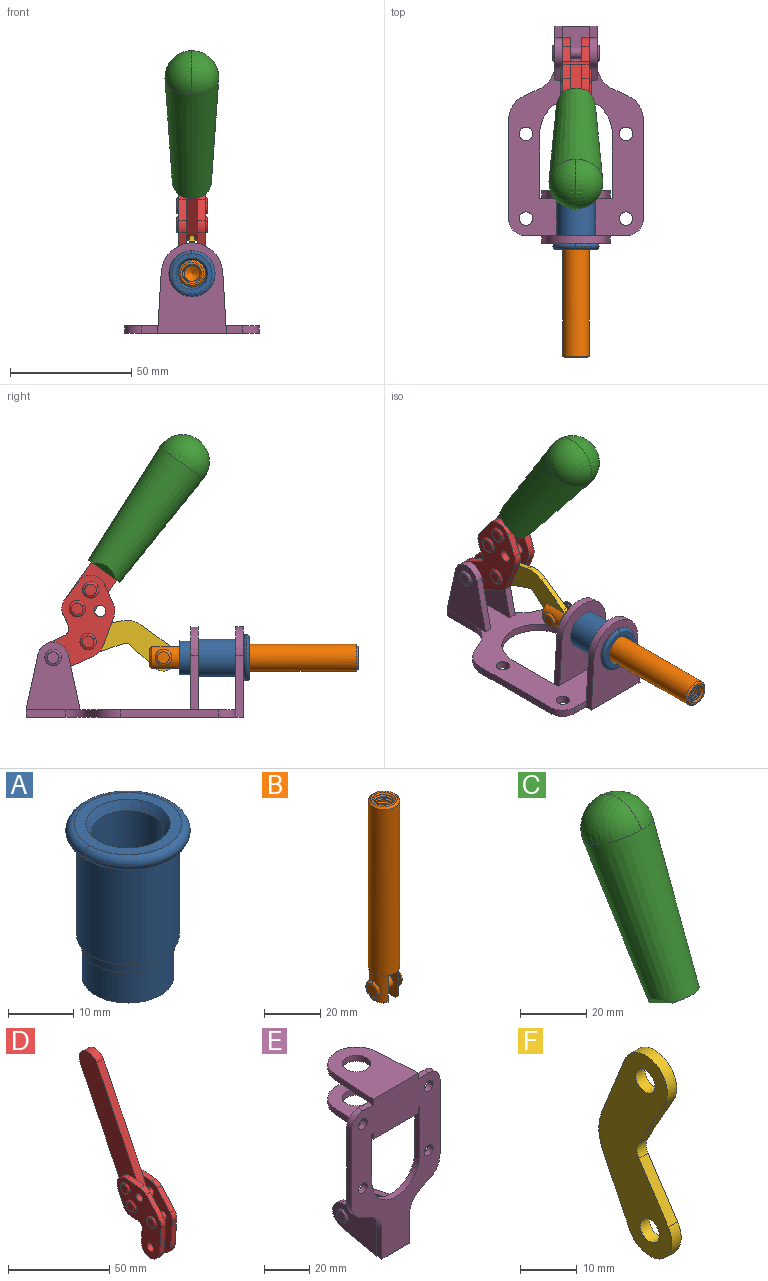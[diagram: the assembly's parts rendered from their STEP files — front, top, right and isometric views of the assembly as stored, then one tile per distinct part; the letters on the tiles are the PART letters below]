
ASSEMBLY  parts=6 mates=6
PART A: 15 faces, bbox 20.6x20.6x28.7 mm
  f0: torus R=8.26mm, axis (0,0,1), area 56.8mm2, adj f1,f10,f12
  f1: torus R=8.26mm, axis (0,0,1), area 56.8mm2, adj f0,f6,f13
  f2: cylinder r=5.59mm len=25.91mm, axis (0,0,1), area 909.6mm2, adj f3,f4
  f3: cone r=6.86mm half-angle=45deg, axis (0,0,-1), area 70.2mm2, adj f2,f14
  f4: cone r=6.47mm half-angle=30deg, axis (0,0,1), area 66.7mm2, adj f2,f13
  f5: cylinder r=7.04mm len=14.07mm, axis (0,0,1), area 252.6mm2, adj f11,f14
  f6: torus R=8.26mm, axis (0,0,1), area 56.8mm2, adj f1,f12,f13
  f7: cylinder r=7.16mm len=14.33mm, axis (0,0,1), area 91.5mm2, adj f9,f11
  f8: cylinder r=7.86mm len=18.42mm, axis (0,0,1), area 909.6mm2, adj f9,f10
  f9: plane 15.72x15.72mm, normal (0,0,-1), area 33mm2, adj f7,f8
  f10: plane 16.51x16.51mm, normal (0,0,-1), area 19.9mm2, adj f0,f8,f12
  f11: plane 14.33x14.33mm, normal (0,0,-1), area 5.7mm2, adj f5,f7
  f12: torus R=8.26mm, axis (0,0,1), area 56.8mm2, adj f0,f6,f10
  f13: plane 16.51x16.51mm, normal (0,0,1), area 82.7mm2, adj f1,f4,f6
  f14: plane 14.07x14.07mm, normal (0,0,-1), area 7.8mm2, adj f3,f5
PART B: 48 faces, bbox 12.6x11.1x86.1 mm
  f0: torus R=2.41mm, axis (-1,0,0), area 15mm2, adj f30,f32,f34
  f1: torus R=2.41mm, axis (-1,0,0), area 15mm2, adj f29,f31,f33
  f2: cylinder r=5.54mm len=72.39mm, axis (0,0,1), area 2518.5mm2, adj f3,f4,f42,f43
  f3: cone r=5.54mm half-angle=45deg, axis (0,0,1), area 7.6mm2, adj f2,f5,f41
  f4: cone r=5.54mm half-angle=45deg, axis (0,0,-1), area 34.9mm2, adj f2,f39
  f5: cylinder r=5.08mm len=11.48mm, axis (0,0,1), area 108.3mm2, adj f3,f7,f8,f41
  f6: cylinder r=2.41mm len=4.83mm, axis (-1,0,0), area 71.2mm2, adj f40,f41
  f7: cylinder r=2.41mm len=4.83mm, axis (-1,0,0), area 7.6mm2, adj f5,f34
  f8: cone r=5.08mm half-angle=45deg, axis (0,0,1), area 10.6mm2, adj f5,f37,f41
  f9: cone r=3.98mm half-angle=45deg, axis (0,0,1), area 17.6mm2, adj f27,f39,f45,f46,f47
  f10: cylinder r=2.41mm len=4.83mm, axis (-1,0,0), area 7.6mm2, adj f33,f38
  f11: cylinder r=3.2mm len=6.4mm, axis (0,0,1), area 78.4mm2, adj f12,f28,f44,f45,f47
  f12: cylinder r=3.2mm len=6.4mm, axis (0,0,1), area 10.5mm2, adj f11,f13,f45,f47
  f13: cylinder r=3.2mm len=6.4mm, axis (0,0,1), area 10.5mm2, adj f12,f14,f45,f47
  f14: cylinder r=3.2mm len=6.4mm, axis (0,0,1), area 10.5mm2, adj f13,f15,f45,f47
  f15: cylinder r=3.2mm len=6.4mm, axis (0,0,1), area 10.5mm2, adj f14,f16,f45,f47
  f16: cylinder r=3.2mm len=6.4mm, axis (0,0,1), area 10.5mm2, adj f15,f17,f45,f47
  f17: cylinder r=3.2mm len=6.4mm, axis (0,0,1), area 10.5mm2, adj f16,f18,f45,f47
  f18: cylinder r=3.2mm len=6.4mm, axis (0,0,1), area 10.5mm2, adj f17,f19,f45,f47
  f19: cylinder r=3.2mm len=6.4mm, axis (0,0,1), area 10.5mm2, adj f18,f20,f45,f47
  f20: cylinder r=3.2mm len=6.4mm, axis (0,0,1), area 10.5mm2, adj f19,f21,f45,f47
  f21: cylinder r=3.2mm len=6.4mm, axis (0,0,1), area 10.5mm2, adj f20,f22,f45,f47
  f22: cylinder r=3.2mm len=6.4mm, axis (0,0,1), area 10.5mm2, adj f21,f23,f45,f47
  f23: cylinder r=3.2mm len=6.4mm, axis (0,0,1), area 10.5mm2, adj f22,f24,f45,f47
  f24: cylinder r=3.2mm len=6.4mm, axis (0,0,1), area 10.5mm2, adj f23,f25,f45,f47
  f25: cylinder r=3.2mm len=6.4mm, axis (0,0,1), area 10.5mm2, adj f24,f26,f45,f47
  f26: cylinder r=3.2mm len=6.4mm, axis (0,0,1), area 10.5mm2, adj f25,f27,f45,f47
  f27: cylinder r=3.2mm len=6.4mm, axis (0,0,1), area 7.4mm2, adj f9,f26,f45,f47
  f28: cone r=3.2mm half-angle=60deg, axis (0,0,1), area 37.2mm2, adj f11
  f29: plane 4.83x4.83mm, normal (-1,0,0), area 18.3mm2, adj f1,f31
  f30: plane 4.83x4.83mm, normal (1,0,0), area 18.3mm2, adj f0,f32
  f31: torus R=2.41mm, axis (-1,0,0), area 15mm2, adj f1,f29,f33
  f32: torus R=2.41mm, axis (-1,0,0), area 15mm2, adj f0,f30,f34
  f33: plane 6.83x6.83mm, normal (1,0,0), area 18.3mm2, adj f1,f10,f31
  f34: plane 6.83x6.83mm, normal (-1,0,0), area 18.3mm2, adj f0,f7,f32
  f35: cone r=5.08mm half-angle=45deg, axis (0,0,1), area 10.6mm2, adj f36,f38,f40
  f36: plane 7.25x1.97mm, normal (0,0,-1), area 10mm2, adj f35,f40
  f37: plane 7.25x1.97mm, normal (0,0,-1), area 10mm2, adj f8,f41
  f38: cylinder r=5.08mm len=11.48mm, axis (0,0,1), area 108.3mm2, adj f10,f35,f40,f42
  f39: plane 9.55x9.55mm, normal (0,0,1), area 22mm2, adj f4,f9
  f40: plane 12.76x10.09mm, normal (1,0,0), area 95.7mm2, adj f6,f35,f36,f38,f42,f43
  f41: plane 12.76x10.09mm, normal (-1,0,0), area 95.7mm2, adj f3,f5,f6,f8,f37,f43
  f42: cone r=5.54mm half-angle=45deg, axis (0,0,1), area 7.6mm2, adj f2,f38,f40
  f43: plane 11.07x4.7mm, normal (0,0,-1), area 50.4mm2, adj f2,f40,f41
  f44: plane 0.89x0.62mm, normal (-1,0,0), area 0.3mm2, adj f11,f45,f46,f47
  f45: bspline ~24.8x7.63mm, area 266.6mm2, adj f9,f11,f12,f13,f14,f15,f16,f17
  f46: bspline ~24.87x7.63mm, area 73.6mm2, adj f9,f44,f45,f47
  f47: bspline ~24.98x7.63mm, area 272.5mm2, adj f9,f11,f12,f13,f14,f15,f16,f17
PART C: 11 faces, bbox 22.3x42.6x64.5 mm
  f0: sphere r=11.13mm, area 411.4mm2, adj f1,f8
  f1: cone r=11.11mm half-angle=3.3deg, axis (0,0.44,0.9), area 3251.8mm2, adj f0,f7,f8,f9,f10
  f2: cylinder r=6.16mm len=11.7mm, axis (1,0,0), area 89.5mm2, adj f3,f4,f5,f6
  f3: plane 60.23x36.75mm, normal (-1,0,0), area 763.6mm2, adj f2,f4,f6,f10
  f4: plane 51.37x25.05mm, normal (0,0.9,-0.44), area 264.2mm2, adj f2,f3,f5,f10
  f5: plane 60.23x36.75mm, normal (1,0,0), area 763.6mm2, adj f2,f4,f6,f10
  f6: plane 51.37x25.05mm, normal (0,-0.9,0.44), area 264.2mm2, adj f2,f3,f5,f10
  f7: plane 9.95x5.95mm, normal (0.71,-0.31,-0.64), area 25.8mm2, adj f1,f10
  f8: sphere r=11.13mm, area 411.4mm2, adj f0,f1
  f9: plane 9.95x5.95mm, normal (-0.71,-0.31,-0.64), area 25.8mm2, adj f1,f10
  f10: plane 14.27x11.38mm, normal (0,-0.44,-0.9), area 106.7mm2, adj f1,f3,f4,f5,f6,f7,f9
PART D: 59 faces, bbox 12.9x60.2x99.6 mm
  f0: torus R=2.39mm, axis (-1,0,0), area 14.9mm2, adj f20,f43,f51
  f1: torus R=2.39mm, axis (-1,0,0), area 14.9mm2, adj f19,f42,f51
  f2: torus R=2.39mm, axis (-1,0,0), area 14.9mm2, adj f18,f35,f51
  f3: torus R=2.39mm, axis (-1,0,0), area 14.9mm2, adj f14,f17,f23
  f4: torus R=2.39mm, axis (-1,0,0), area 14.9mm2, adj f13,f16,f23
  f5: torus R=2.39mm, axis (-1,0,0), area 14.9mm2, adj f12,f15,f23
  f6: cylinder r=2.39mm len=4.78mm, axis (1,0,0), area 46.5mm2, adj f48,f50,f51
  f7: cylinder r=2.39mm len=4.78mm, axis (1,0,0), area 46.5mm2, adj f50,f51
  f8: cylinder r=6.35mm len=12.68mm, axis (1,0,0), area 61.8mm2, adj f38,f39,f50,f51
  f9: cylinder r=2.39mm len=4.78mm, axis (-1,0,0), area 70.5mm2, adj f46,f50
  f10: cylinder r=2.39mm len=4.78mm, axis (-1,0,0), area 46.5mm2, adj f23,f45,f46
  f11: cylinder r=2.39mm len=4.78mm, axis (-1,0,0), area 46.5mm2, adj f23,f46
  f12: plane 4.78x4.78mm, normal (1,0,0), area 17.9mm2, adj f5,f15
  f13: plane 4.78x4.78mm, normal (1,0,0), area 17.9mm2, adj f4,f16
  f14: plane 4.78x4.78mm, normal (1,0,0), area 17.9mm2, adj f3,f17
  f15: torus R=2.39mm, axis (-1,0,0), area 14.9mm2, adj f5,f12,f23
  f16: torus R=2.39mm, axis (-1,0,0), area 14.9mm2, adj f4,f13,f23
  f17: torus R=2.39mm, axis (-1,0,0), area 14.9mm2, adj f3,f14,f23
  f18: plane 4.78x4.78mm, normal (-1,0,0), area 17.9mm2, adj f2,f35
  f19: plane 4.78x4.78mm, normal (-1,0,0), area 17.9mm2, adj f1,f42
  f20: plane 4.78x4.78mm, normal (-1,0,0), area 17.9mm2, adj f0,f43
  f21: plane 2.26x0.2mm, normal (1,0,0), area 0.2mm2, adj f31,f44
  f22: plane 2.26x0.2mm, normal (-1,0,0), area 0.2mm2, adj f41,f44
  f23: plane 39.37x30.77mm, normal (1,0,0), area 565.5mm2, adj f3,f4,f5,f10,f11,f15,f16,f17
  f24: cylinder r=6.1mm len=4.15mm, axis (-1,0,0), area 14.7mm2, adj f23,f25,f32,f46
  f25: plane 10.25x9.01mm, normal (0,-0.75,0.66), area 42.3mm2, adj f23,f24,f26,f46
  f26: cylinder r=6.35mm len=4.64mm, axis (-1,0,0), area 15.6mm2, adj f23,f25,f27,f46
  f27: plane 15.84x3.1mm, normal (0,-1,-0.07), area 49.2mm2, adj f23,f26,f28,f46
  f28: cylinder r=6.35mm len=12.68mm, axis (-1,0,0), area 61.8mm2, adj f23,f27,f29,f46
  f29: plane 8.11x3.1mm, normal (0,1,0.07), area 25.2mm2, adj f23,f28,f30,f46
  f30: cylinder r=3.05mm len=3.25mm, axis (-1,0,0), area 14.8mm2, adj f23,f29,f31,f46
  f31: plane 5.99x3.1mm, normal (0,0.07,-1), area 18.6mm2, adj f21,f23,f30,f44,f46
  f32: plane 9.5x3.1mm, normal (0,-0.07,1), area 29.5mm2, adj f23,f24,f33,f46,f47
  f33: cylinder r=6.1mm len=8.63mm, axis (-1,0,0), area 39.1mm2, adj f23,f32,f34,f47
  f34: plane 8.65x3.96mm, normal (0,0.91,-0.42), area 29.5mm2, adj f23,f33,f44,f47
  f35: torus R=2.39mm, axis (-1,0,0), area 14.9mm2, adj f2,f18,f51
  f36: plane 10.25x9.01mm, normal (0,-0.75,0.66), area 42.3mm2, adj f37,f49,f50,f51
  f37: cylinder r=6.35mm len=4.64mm, axis (1,0,0), area 15.6mm2, adj f36,f38,f50,f51
  f38: plane 15.84x3.1mm, normal (0,-1,-0.07), area 49.2mm2, adj f8,f37,f50,f51
  f39: plane 8.11x3.1mm, normal (0,1,0.07), area 25.2mm2, adj f8,f40,f50,f51
  f40: cylinder r=3.05mm len=3.25mm, axis (1,0,0), area 14.8mm2, adj f39,f41,f50,f51
  f41: plane 5.99x3.1mm, normal (0,0.07,-1), area 18.6mm2, adj f22,f40,f44,f50,f51
  f42: torus R=2.39mm, axis (-1,0,0), area 14.9mm2, adj f1,f19,f51
  f43: torus R=2.39mm, axis (-1,0,0), area 14.9mm2, adj f0,f20,f51
  f44: cylinder r=6.35mm len=12.12mm, axis (-1,0,0), area 128.9mm2, adj f21,f22,f23,f31,f34,f41,f46,f47
  f45: plane 2.65x1.35mm, normal (1,0,0), area 1mm2, adj f10,f55
  f46: plane 39.08x20.42mm, normal (-1,0,0), area 412.5mm2, adj f9,f10,f11,f24,f25,f26,f27,f28
  f47: plane 77.62x39.82mm, normal (1,0,0), area 850mm2, adj f32,f33,f34,f44,f53,f54,f55
  f48: plane 2.65x1.35mm, normal (-1,0,0), area 1mm2, adj f6,f55
  f49: cylinder r=6.1mm len=4.15mm, axis (1,0,0), area 14.7mm2, adj f36,f50,f51,f56
  f50: plane 39.08x20.42mm, normal (1,0,0), area 412.5mm2, adj f6,f7,f8,f9,f36,f37,f38,f39
  f51: plane 39.37x30.77mm, normal (-1,0,0), area 565.5mm2, adj f0,f1,f2,f6,f7,f8,f35,f36
  f52: plane 8.65x3.96mm, normal (0,0.91,-0.42), area 29.5mm2, adj f44,f51,f57,f58
  f53: plane 68.49x33.4mm, normal (0,0.9,-0.44), area 358.1mm2, adj f44,f47,f54,f58
  f54: cylinder r=6.35mm len=12.06mm, axis (1,0,0), area 93.7mm2, adj f47,f53,f55,f58
  f55: plane 68.49x33.4mm, normal (0,-0.9,0.44), area 358.1mm2, adj f44,f45,f46,f47,f48,f50,f54,f58
  f56: plane 9.5x3.1mm, normal (0,-0.07,1), area 29.5mm2, adj f49,f50,f51,f57,f58
  f57: cylinder r=6.1mm len=8.63mm, axis (1,0,0), area 39.1mm2, adj f51,f52,f56,f58
  f58: plane 77.62x39.82mm, normal (-1,0,0), area 850mm2, adj f44,f52,f53,f54,f55,f56,f57
PART E: 55 faces, bbox 55.7x37.4x89.8 mm
  f0: torus R=2.41mm, axis (-1,0,0), area 15mm2, adj f11,f15,f25
  f1: torus R=2.41mm, axis (-1,0,0), area 15mm2, adj f10,f12,f22
  f2: cylinder r=2.78mm len=5.56mm, axis (0,-1,0), area 54.2mm2, adj f30,f54
  f3: cylinder r=14.99mm len=29.97mm, axis (0,-1,0), area 145.9mm2, adj f30,f49,f53,f54
  f4: cylinder r=2.78mm len=5.56mm, axis (0,-1,0), area 54.2mm2, adj f30,f54
  f5: cylinder r=2.78mm len=5.56mm, axis (0,-1,0), area 54.2mm2, adj f30,f54
  f6: cylinder r=2.78mm len=5.56mm, axis (0,-1,0), area 54.2mm2, adj f30,f54
  f7: cylinder r=6.35mm len=12.7mm, axis (0,0,1), area 123.6mm2, adj f27,f51
  f8: cylinder r=6.35mm len=12.7mm, axis (0,0,-1), area 124.7mm2, adj f21,f35
  f9: cylinder r=2.41mm len=11.18mm, axis (-1,0,0), area 169.4mm2, adj f16,f19
  f10: plane 4.83x4.83mm, normal (1,0,0), area 18.3mm2, adj f1,f12
  f11: plane 4.83x4.83mm, normal (-1,0,0), area 18.3mm2, adj f0,f15
  f12: torus R=2.41mm, axis (-1,0,0), area 15mm2, adj f1,f10,f22
  f13: cylinder r=6.35mm len=12.41mm, axis (1,0,0), area 53.4mm2, adj f18,f19,f22,f23
  f14: cylinder r=6.35mm len=12.41mm, axis (-1,0,0), area 53.4mm2, adj f16,f17,f24,f25
  f15: torus R=2.41mm, axis (-1,0,0), area 15mm2, adj f0,f11,f25
  f16: plane 27.86x22.35mm, normal (1,0,0), area 425.4mm2, adj f9,f14,f17,f24,f30
  f17: plane 22.86x4.97mm, normal (0,0.21,0.98), area 72.5mm2, adj f14,f16,f25,f30
  f18: plane 22.86x4.97mm, normal (0,0.21,0.98), area 72.5mm2, adj f13,f19,f22,f30
  f19: plane 27.86x22.35mm, normal (-1,0,0), area 425.4mm2, adj f9,f13,f18,f23,f30
  f20: cylinder r=12.7mm len=25.35mm, axis (0,0,-1), area 119.8mm2, adj f21,f34,f35,f36
  f21: plane 34.21x28.07mm, normal (0,0,-1), area 702.4mm2, adj f8,f20,f30,f34,f36
  f22: plane 27.96x22.45mm, normal (1,0,0), area 407.2mm2, adj f1,f12,f13,f18,f23,f30,f42,f43
  f23: plane 22.86x4.97mm, normal (0,0.21,-0.98), area 72.5mm2, adj f13,f19,f22,f44
  f24: plane 22.86x4.97mm, normal (0,0.21,-0.98), area 72.5mm2, adj f14,f16,f25,f44
  f25: plane 27.86x22.35mm, normal (-1,0,0), area 407.1mm2, adj f0,f14,f15,f17,f24,f30,f45,f46
  f26: plane 3.1x0.95mm, normal (0,0,-1), area 2.7mm2, adj f30,f49,f50,f54
  f27: plane 34.21x28.07mm, normal (0,0,1), area 702.4mm2, adj f7,f28,f30,f50,f52
  f28: cylinder r=12.7mm len=25.35mm, axis (0,0,1), area 118.8mm2, adj f27,f50,f51,f52
  f29: plane 3.1x0.95mm, normal (0,0,-1), area 2.7mm2, adj f30,f52,f53,f54
  f30: plane 86.54x55.63mm, normal (0,1,0), area 2362.9mm2, adj f2,f3,f4,f5,f6,f16,f17,f18
  f31: plane 40.56x3.1mm, normal (-1,0,0), area 125.7mm2, adj f30,f32,f48,f54
  f32: cylinder r=7.11mm len=7.11mm, axis (0,-1,0), area 34.6mm2, adj f30,f31,f33,f54
  f33: plane 6.67x3.1mm, normal (0,0,1), area 20.4mm2, adj f30,f32,f34,f54
  f34: plane 25.39x3.13mm, normal (-1,0.06,0), area 79.5mm2, adj f20,f21,f33,f35,f54
  f35: plane 37.31x28.45mm, normal (0,0,1), area 789.9mm2, adj f8,f20,f34,f36,f54
  f36: plane 25.39x3.13mm, normal (1,0.06,0), area 79.5mm2, adj f20,f21,f35,f37,f54
  f37: plane 6.67x3.1mm, normal (0,0,1), area 20.4mm2, adj f30,f36,f38,f54
  f38: cylinder r=7.11mm len=7.11mm, axis (0,-1,0), area 34.6mm2, adj f30,f37,f39,f54
  f39: plane 40.56x3.1mm, normal (1,0,0), area 125.7mm2, adj f30,f38,f40,f54
  f40: cylinder r=11.18mm len=10.16mm, axis (0,-1,0), area 39.5mm2, adj f30,f39,f41,f54
  f41: plane 6.09x3.1mm, normal (0.42,0,-0.91), area 20.8mm2, adj f30,f40,f42,f54
  f42: cylinder r=11.18mm len=9.41mm, axis (0,-1,0), area 37.2mm2, adj f22,f30,f41,f43,f54
  f43: plane 16.5x3.1mm, normal (1,0,0), area 51.1mm2, adj f22,f42,f44,f54
  f44: plane 17.37x3.1mm, normal (0,0,-1), area 53.8mm2, adj f23,f24,f30,f43,f45,f54
  f45: plane 16.5x3.1mm, normal (-1,0,0), area 51.1mm2, adj f25,f44,f46,f54
  f46: cylinder r=11.18mm len=9.41mm, axis (0,-1,0), area 37.2mm2, adj f25,f30,f45,f47,f54
  f47: plane 6.09x3.1mm, normal (-0.42,0,-0.91), area 20.8mm2, adj f30,f46,f48,f54
  f48: cylinder r=11.18mm len=10.16mm, axis (0,-1,0), area 39.5mm2, adj f30,f31,f47,f54
  f49: plane 26.54x3.1mm, normal (-1,0,0), area 82.3mm2, adj f3,f26,f30,f54
  f50: plane 25.39x3.1mm, normal (1,0.06,0), area 78.8mm2, adj f26,f27,f28,f51,f54
  f51: plane 37.31x28.45mm, normal (0,0,-1), area 789.9mm2, adj f7,f28,f50,f52,f54
  f52: plane 25.39x3.1mm, normal (-1,0.06,0), area 78.8mm2, adj f27,f28,f29,f51,f54
  f53: plane 26.54x3.1mm, normal (1,0,0), area 82.3mm2, adj f3,f29,f30,f54
  f54: plane 89.66x55.63mm, normal (0,-1,0), area 2678.5mm2, adj f2,f3,f4,f5,f6,f26,f29,f31
PART F: 12 faces, bbox 2.3x18.2x42.8 mm
  f0: cylinder r=2.4mm len=4.8mm, axis (1,0,0), area 34.9mm2, adj f4,f11
  f1: cylinder r=10.41mm len=8.47mm, axis (1,0,0), area 20.2mm2, adj f4,f9,f10,f11
  f2: cylinder r=3.05mm len=3.16mm, axis (1,0,0), area 7.7mm2, adj f4,f6,f7,f11
  f3: cylinder r=2.4mm len=4.8mm, axis (1,0,0), area 34.9mm2, adj f4,f11
  f4: plane 42.81x18.23mm, normal (-1,0,0), area 414.1mm2, adj f0,f1,f2,f3,f5,f6,f7,f8
  f5: cylinder r=5.54mm len=10.67mm, axis (1,0,0), area 41.8mm2, adj f4,f6,f10,f11
  f6: plane 11.66x6.53mm, normal (0,-0.87,-0.49), area 30.9mm2, adj f2,f4,f5,f11
  f7: plane 11.17x7.33mm, normal (0,-0.84,0.55), area 30.9mm2, adj f2,f4,f8,f11
  f8: cylinder r=5.54mm len=10.51mm, axis (1,0,0), area 41.8mm2, adj f4,f7,f9,f11
  f9: plane 13.67x6.67mm, normal (0,0.9,-0.44), area 35.1mm2, adj f1,f4,f8,f11
  f10: plane 14.1x5.7mm, normal (0,0.93,0.37), area 35.1mm2, adj f1,f4,f5,f11
  f11: plane 42.81x18.23mm, normal (1,0,0), area 414.1mm2, adj f0,f1,f2,f3,f5,f6,f7,f8
PLACE A rot(axis=(0.58,0.58,-0.58),120deg) t=(-21.91,2.7,23.91)mm
PLACE B rot(axis=(1,0,0),90deg) t=(2.7,4.75,-0.7)mm
PLACE C rot(axis=(1,0,0),61.6deg) t=(2.66,-5.15,17.54)mm
PLACE D rot(axis=(1,0,0),61.6deg) t=(2.7,-5.15,17.54)mm
PLACE E rot(axis=(1,0,0),90deg) t=(2.7,2.7,-0.7)mm fixed
PLACE F rot(axis=(1,0,0),103.9deg) t=(2.7,10.22,3.75)mm
MATE revolute F.f3 <-> D.f4  axis (1,0,0) through (2.7,20.34,30.47)mm
MATE fastened C.f2 <-> D.f54  axis (1,0,0) through (0.35,-19.51,106.09)mm
MATE slider B.f2 <-> E.f7  axis (0,-1,0) through (2.7,-54.03,23.91)mm
MATE fastened A.f0 <-> E.f7  axis (0,1,0) through (2.7,-43.69,23.91)mm
MATE revolute D.f7 <-> E.f0  axis (1,0,0) through (2.7,34.79,23.91)mm
MATE revolute F.f5 <-> B.f6  axis (1,0,0) through (2.7,-10.73,23.91)mm
